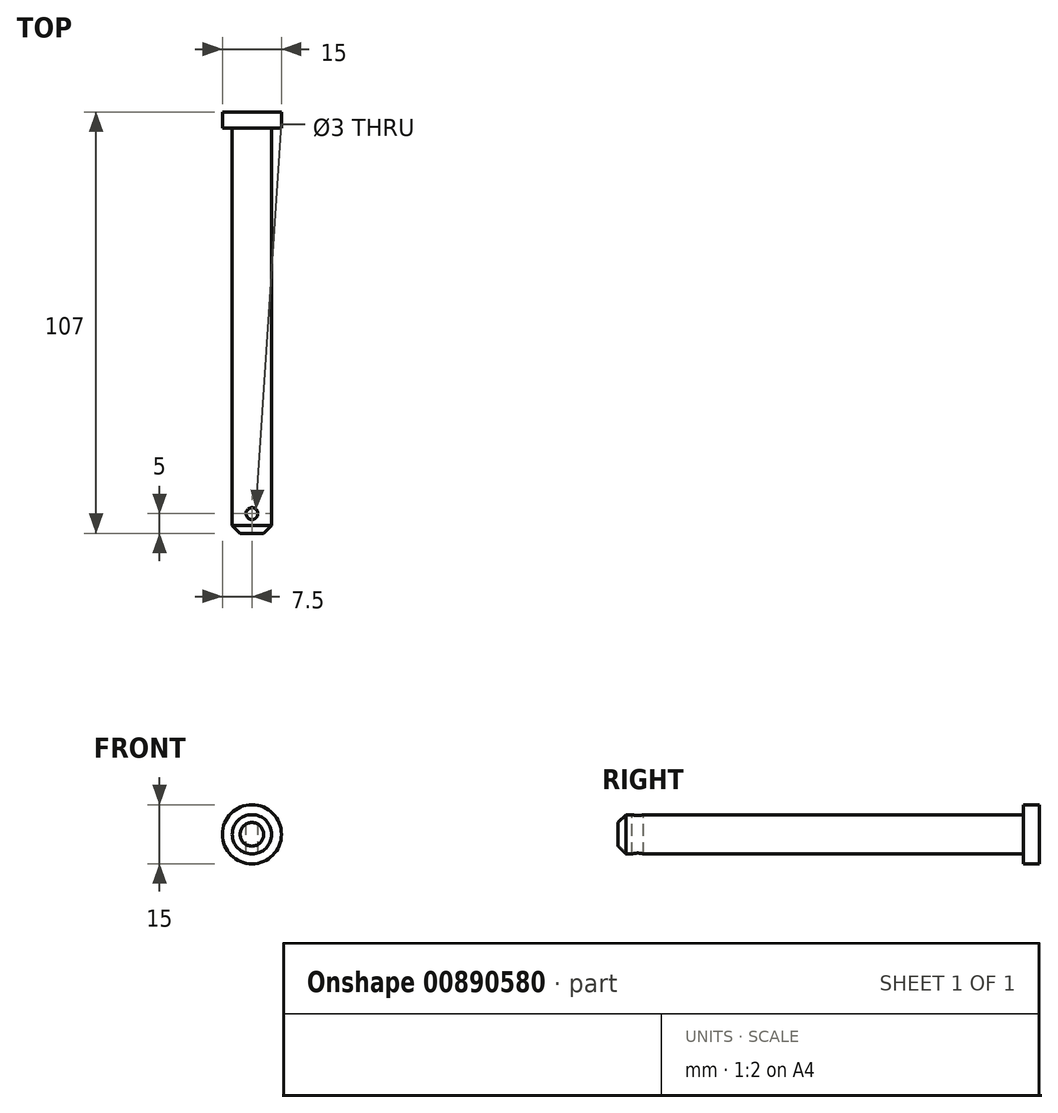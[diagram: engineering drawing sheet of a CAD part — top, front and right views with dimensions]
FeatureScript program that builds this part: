
annotation { "Feature Type Name" : "Feature", "Feature Type Description" : "" }
export const myFeature = defineFeature(function(context is Context, id is Id, definition is map)
    precondition{}
    {
        {
            var Q0;
            Q0=qCreatedBy(makeId("Front.planeOp"),FACE);
            var sketch = newSketch(context, id + "F0", { "sketchPlane" : qUnion([Q0])});
            skCircle(sketch, "E0", {"center": v(0, 0) * mm, "radius": 7.5 * mm});
            skSolve(sketch);
        }
        {
            var Q0;
            Q0 = qSketchRegion(id + "F0", true);
            extrude(context, id + "F1", {"entities" : qUnion([Q0]), "depth" : 4 * mm, "offsetDistance" : 25 * mm});
        }
        {
            var Q0;
            Q0=makeQuery(id+"F1.opExtrude","CAP_FACE",FACE,{"disambiguationData":[OSD([sQuery(id+"F0.wireOp",EDGE,"E0")])],"isStart":false});
            var sketch = newSketch(context, id + "F2", { "sketchPlane" : qUnion([Q0])});
            skCircle(sketch, "E1", {"center": v(0, 0) * mm, "radius": 5 * mm});
            skSolve(sketch);
        }
        {
            var Q0;
            Q0 = qSketchRegion(id + "F2", true);
            extrude(context, id + "F3", {"entities" : qUnion([Q0]), "operationType" : NewBodyOperationType.ADD, "depth" : (85 + 8 + 10) * mm, "offsetDistance" : 25 * mm});
        }
        {
            var Q0;
            Q0=qCreatedBy(makeId("Top.planeOp"),FACE);
            var sketch = newSketch(context, id + "F4", { "sketchPlane" : qUnion([Q0])});
            skCircle(sketch, "E2", {"center": v(0, -102) * mm, "radius": 1.5 * mm});
            skSolve(sketch);
        }
        {
            var Q0;
            Q0 = qSketchRegion(id + "F4", true);
            extrude(context, id + "F5", {"entities" : qUnion([Q0]), "operationType" : NewBodyOperationType.REMOVE, "endBound" : BoundingType.SYMMETRIC, "oppositeDirection" : true, "depth" : 25 * mm, "offsetDistance" : 25 * mm});
        }
        {
            var Q0;
            Q0=makeQuery(id+"F3.opExtrude","CAP_EDGE",EDGE,{"disambiguationData":[OSD([sQuery(id+"F2.wireOp",EDGE,"E1")])],"isStart":false});
            chamfer(context, id + "F6", {"entities" : qUnion([Q0]), "width" : 2 * mm, "tangentPropagation" : true});
        }
    });
